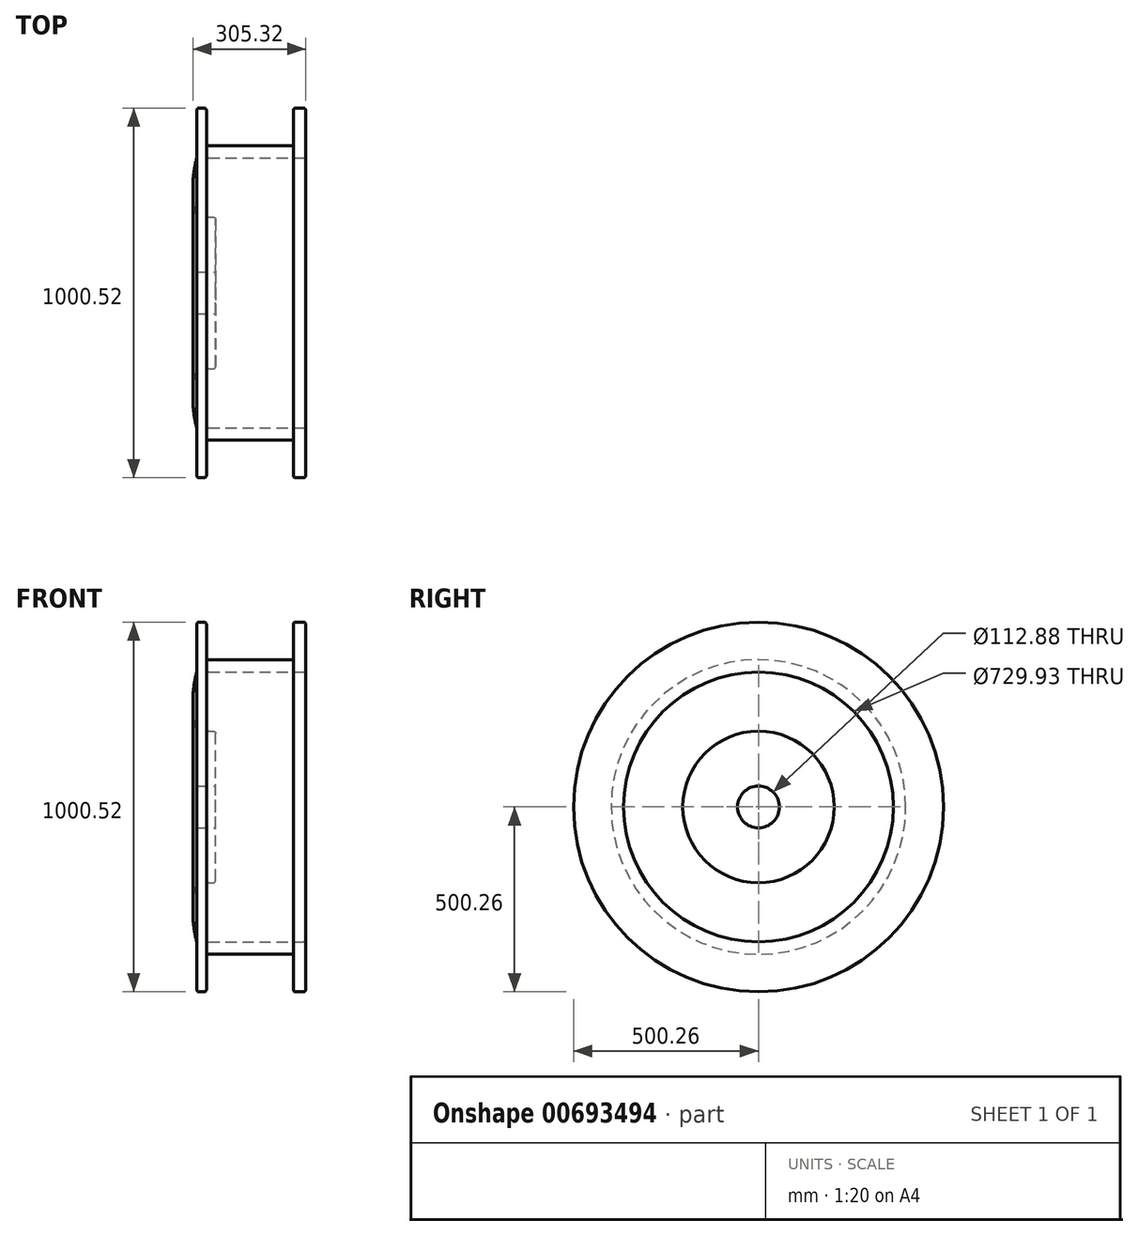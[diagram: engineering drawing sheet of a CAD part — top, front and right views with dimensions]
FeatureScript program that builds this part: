
annotation { "Feature Type Name" : "Feature", "Feature Type Description" : "" }
export const myFeature = defineFeature(function(context is Context, id is Id, definition is map)
    precondition{}
    {
        {
            var Q0;
            Q0=qCreatedBy(makeId("Front.planeOp"),FACE);
            var sketch = newSketch(context, id + "F0", { "sketchPlane" : qUnion([Q0])});
            skArc(sketch, "E0", {"start": v(-50.8, 364.96) * mm, "mid": v(-61.54, 284.93) * mm, "end": v(-50.8, 204.9) * mm});
            skLineSegment(sketch, "E1", {"start": v(-50.8, 364.96) * mm, "end": v(-50.8, 493.9) * mm});
            skLineSegment(sketch, "E2", {"start": v(-44.45, 500.26) * mm, "end": v(-31.13, 500.26) * mm});
            skLineSegment(sketch, "E3", {"start": v(-24.78, 493.87) * mm, "end": v(-25.32, 404.91) * mm});
            skLineSegment(sketch, "E4", {"start": v(-25.36, 358.61) * mm, "end": v(-25.36, 211.25) * mm});
            skLineSegment(sketch, "E5", {"start": v(-19, 204.9) * mm, "end": v(-6.35, 204.9) * mm});
            skLineSegment(sketch, "E6", {"start": v(287.06, 0) * mm, "end": v(-195.02, 0) * mm});
            skPoint(sketch, "E7.visualSharp", {"position": v(-50.8, 500.26) * mm});
            skArc(sketch, "E7.filletArc", {"start": v(-44.45, 500.26) * mm, "mid": v(-48.94, 498.4) * mm, "end": v(-50.8, 493.9) * mm});
            skPoint(sketch, "E8.visualSharp", {"position": v(-24.74, 500.26) * mm});
            skArc(sketch, "E8.filletArc", {"start": v(-24.78, 493.87) * mm, "mid": v(-26.62, 498.38) * mm, "end": v(-31.13, 500.26) * mm});
            skPoint(sketch, "E9.visualSharp", {"position": v(-25.36, 398.52) * mm});
            skArc(sketch, "E9.filletArc", {"start": v(-25.32, 404.91) * mm, "mid": v(-23.47, 400.4) * mm, "end": v(-18.97, 398.52) * mm});
            skPoint(sketch, "E10.visualSharp", {"position": v(-25.36, 204.9) * mm});
            skArc(sketch, "E10.filletArc", {"start": v(-25.36, 211.25) * mm, "mid": v(-23.5, 206.76) * mm, "end": v(-19, 204.9) * mm});
            skPoint(sketch, "E11.visualSharp", {"position": v(-50.8, 128.7) * mm});
            skPoint(sketch, "E12.visualSharp", {"position": v(0, 204.9) * mm});
            skArc(sketch, "E12.filletArc", {"start": v(0, 198.55) * mm, "mid": v(-1.86, 203.05) * mm, "end": v(-6.35, 204.9) * mm});
            skPoint(sketch, "E13.visualSharp", {"position": v(0, 128.7) * mm});
            skPoint(sketch, "E14.end.orphan", {"position": v(141.35, 500.26) * mm});
            skPoint(sketch, "E15.start.orphan", {"position": v(170.34, 364.96) * mm});
            skLineSegment(sketch, "E16", {"start": v(-18.97, 398.52) * mm, "end": v(210.12, 398.52) * mm});
            skLineSegment(sketch, "E17", {"start": v(210.12, 398.52) * mm, "end": v(210.12, 493.9) * mm});
            skLineSegment(sketch, "E18", {"start": v(216.47, 500.26) * mm, "end": v(237.43, 500.26) * mm});
            skLineSegment(sketch, "E19", {"start": v(243.78, 493.9) * mm, "end": v(243.78, 371.31) * mm});
            skLineSegment(sketch, "E20", {"start": v(237.43, 364.96) * mm, "end": v(-19, 364.96) * mm});
            skPoint(sketch, "E21.visualSharp", {"position": v(210.12, 500.26) * mm});
            skArc(sketch, "E21.filletArc", {"start": v(216.47, 500.26) * mm, "mid": v(211.98, 498.4) * mm, "end": v(210.12, 493.9) * mm});
            skPoint(sketch, "E22.visualSharp", {"position": v(243.78, 364.96) * mm});
            skArc(sketch, "E22.filletArc", {"start": v(237.43, 364.96) * mm, "mid": v(241.92, 366.82) * mm, "end": v(243.78, 371.31) * mm});
            skPoint(sketch, "E23.visualSharp", {"position": v(-25.36, 364.96) * mm});
            skArc(sketch, "E23.filletArc", {"start": v(-19, 364.96) * mm, "mid": v(-23.5, 363.1) * mm, "end": v(-25.36, 358.61) * mm});
            skPoint(sketch, "E24.visualSharp", {"position": v(243.78, 500.26) * mm});
            skArc(sketch, "E24.filletArc", {"start": v(243.78, 493.9) * mm, "mid": v(241.92, 498.4) * mm, "end": v(237.43, 500.26) * mm});
            skLineSegment(sketch, "E25", {"start": v(-50.8, 204.9) * mm, "end": v(-50.8, 56.44) * mm});
            skLineSegment(sketch, "E26", {"start": v(-50.8, 56.44) * mm, "end": v(0, 56.44) * mm});
            skLineSegment(sketch, "E27", {"start": v(0, 56.44) * mm, "end": v(0, 198.55) * mm});
            skSolve(sketch);
        }
        {
            var Q0;
            Q0 = qSketchRegion(id + "F0", true);
            var Q1;
            Q1=sQuery(id+"F0.wireOp",EDGE,"E6");
            revolve(context, id + "F1", {"entities" : qUnion([Q0]), "axis" : qUnion([Q1]), "revolveType" : RevolveType.FULL});
        }
    });
